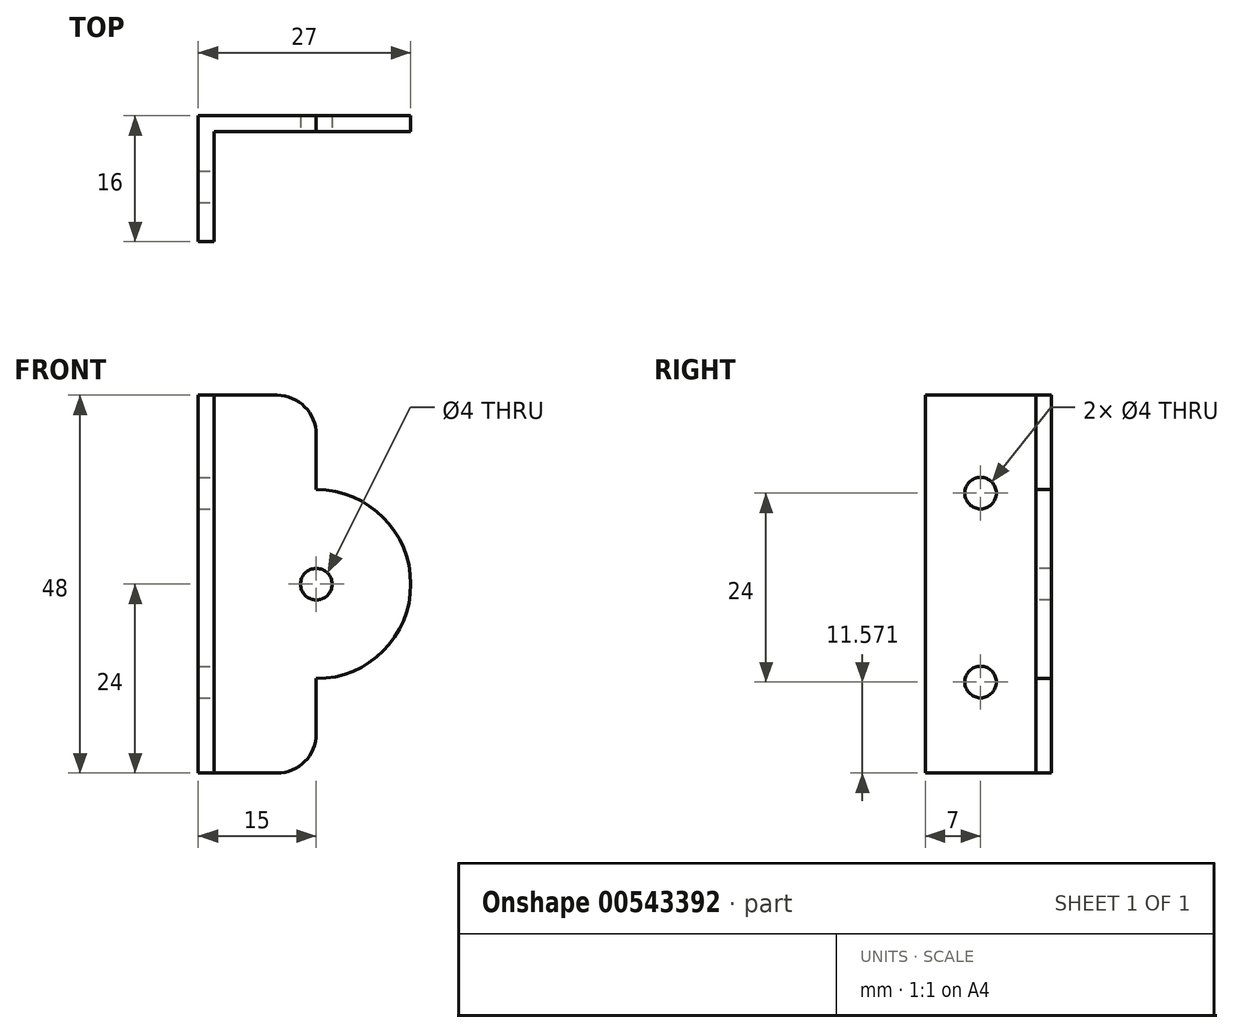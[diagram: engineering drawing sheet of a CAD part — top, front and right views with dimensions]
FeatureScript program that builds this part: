
annotation { "Feature Type Name" : "Feature", "Feature Type Description" : "" }
export const myFeature = defineFeature(function(context is Context, id is Id, definition is map)
    precondition{}
    {
        {
            var Q0;
            Q0=qCreatedBy(makeId("Front.planeOp"),FACE);
            var sketch = newSketch(context, id + "F0", { "sketchPlane" : qUnion([Q0])});
            skLineSegment(sketch, "E0.bottom", {"start": v(-7.5, -24) * mm, "end": v(2.5, -24) * mm});
            skLineSegment(sketch, "E0.top", {"start": v(-7.5, 24) * mm, "end": v(2.5, 24) * mm});
            skLineSegment(sketch, "E0.left", {"start": v(-7.5, -24) * mm, "end": v(-7.5, 24) * mm});
            skLineSegment(sketch, "E0.right", {"start": v(7.5, -19) * mm, "end": v(7.5, 19) * mm});
            skPoint(sketch, "E0.middle", {"position": v(0, 0) * mm});
            skLineSegment(sketch, "E1", {"start": v(-5.5, 24) * mm, "end": v(-5.5, -24) * mm});
            skArc(sketch, "E2", {"start": v(7.5, -12) * mm, "mid": v(19.5, 0) * mm, "end": v(7.5, 12) * mm});
            skPoint(sketch, "E3.visualSharp", {"position": v(7.5, 24) * mm});
            skArc(sketch, "E3.filletArc", {"start": v(7.5, 19) * mm, "mid": v(6.04, 22.54) * mm, "end": v(2.5, 24) * mm});
            skPoint(sketch, "E4.visualSharp", {"position": v(7.5, -24) * mm});
            skArc(sketch, "E4.filletArc", {"start": v(2.5, -24) * mm, "mid": v(6.04, -22.54) * mm, "end": v(7.5, -19) * mm});
            skPoint(sketch, "E5", {"position": v(19.5, 0) * mm});
            skPoint(sketch, "E6", {"position": v(10.94, 0) * mm});
            skSolve(sketch);
        }
        {
            var Q0;
            {var subQ0=sQuery(id+"F0.wireOp",EDGE,"E0.left");Q0=makeQuery(id+"F0.imprint","IMPRINT",FACE,{"disambiguationData":[TD([[makeQuery(id+"F0.imprint","IMPRINT",EDGE,{"derivedFrom":subQ0}),-1.0]])]});}
            extrude(context, id + "F1", {"entities" : qUnion([Q0]), "depth" : 16 * mm, "offsetDistance" : 25 * mm});
        }
        {
            var Q0;
            Q0 = qSketchRegion(id + "F0", true);
            extrude(context, id + "F2", {"entities" : qUnion([Q0]), "operationType" : NewBodyOperationType.ADD, "depth" : 2 * mm, "offsetDistance" : 25 * mm});
        }
        {
            var Q0;
            Q0=makeQuery(id+"F2.opExtrude","CAP_FACE",FACE,{"disambiguationData":[OSD([sQuery(id+"F0.wireOp",EDGE,"E0.bottom"),sQuery(id+"F0.wireOp",EDGE,"E0.top"),sQuery(id+"F0.wireOp",EDGE,"E0.left"),sQuery(id+"F0.wireOp",EDGE,"E0.right"),sQuery(id+"F0.wireOp",EDGE,"E2"),sQuery(id+"F0.wireOp",EDGE,"E3.filletArc"),sQuery(id+"F0.wireOp",EDGE,"E4.filletArc")])],"isStart":false});
            var sketch = newSketch(context, id + "F3", { "sketchPlane" : qUnion([Q0])});
            skPoint(sketch, "E7", {"position": v(7.5, 0) * mm});
            skSolve(sketch);
        }
        {
            var Q0;
            Q0=sQuery(id+"F3.wireOp",VERTEX,"E7");
            var Q1;
            Q1=makeQuery(id+"F1.opExtrude","SWEPT_BODY",BODY,{"disambiguationData":[OSD([sQuery(id+"F0.wireOp",EDGE,"E0.bottom"),sQuery(id+"F0.wireOp",EDGE,"E0.top"),sQuery(id+"F0.wireOp",EDGE,"E0.left"),sQuery(id+"F0.wireOp",EDGE,"E1")])]});
            hole(context, id + "F4", {"style" : HoleStyle.SIMPLE, "endStyle" : HoleEndStyle.THROUGH, "holeDiameter" : 4 * mm, "isTappedThrough" : true, "tappedDepth" : 12 * mm, "tapClearance" : 3, "locations" : qUnion([Q0]), "scope" : qUnion([Q1])});
        }
        {
            var Q0;
            Q0=makeQuery(id+"F1.opExtrude","SWEPT_FACE",FACE,{"disambiguationData":[OSD([sQuery(id+"F0.wireOp",EDGE,"E1")])]});
            var sketch = newSketch(context, id + "F5", { "sketchPlane" : qUnion([Q0])});
            skPoint(sketch, "E8", {"position": v(-9, 11.57) * mm});
            skPoint(sketch, "E9", {"position": v(-9, -12.43) * mm});
            skSolve(sketch);
        }
        {
            var Q0;
            Q0=sQuery(id+"F5.wireOp",VERTEX,"E9");
            var Q1;
            Q1=sQuery(id+"F5.wireOp",VERTEX,"E8");
            var Q2;
            Q2=makeQuery(id+"F1.opExtrude","SWEPT_BODY",BODY,{"disambiguationData":[OSD([sQuery(id+"F0.wireOp",EDGE,"E0.bottom"),sQuery(id+"F0.wireOp",EDGE,"E0.top"),sQuery(id+"F0.wireOp",EDGE,"E0.left"),sQuery(id+"F0.wireOp",EDGE,"E1")])]});
            hole(context, id + "F6", {"style" : HoleStyle.SIMPLE, "endStyle" : HoleEndStyle.THROUGH, "holeDiameter" : 4 * mm, "isTappedThrough" : true, "tappedDepth" : 12 * mm, "tapClearance" : 3, "locations" : qUnion([Q0, Q1]), "scope" : qUnion([Q2])});
        }
    });
